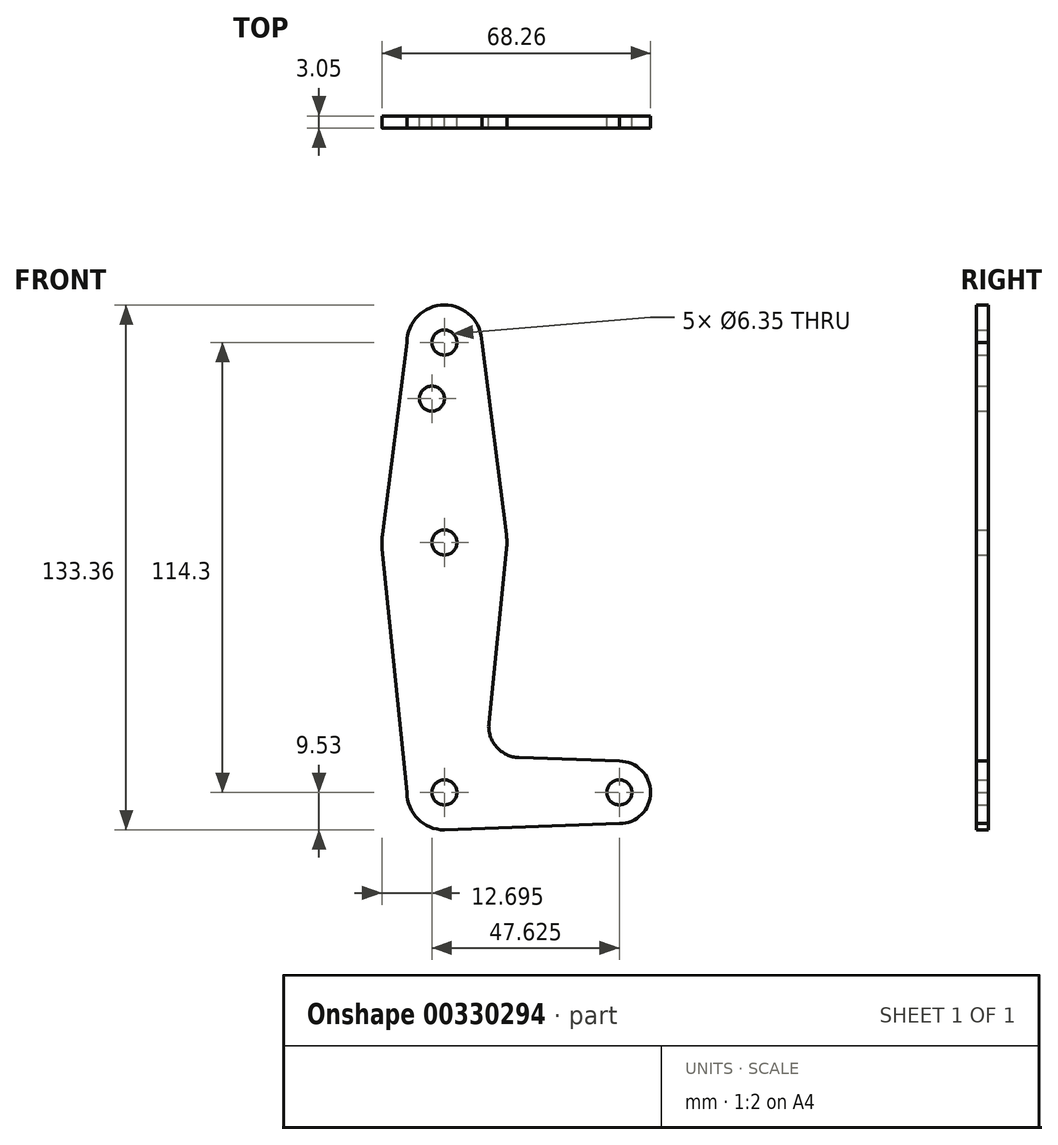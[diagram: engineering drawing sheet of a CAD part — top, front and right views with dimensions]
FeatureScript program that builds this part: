
annotation { "Feature Type Name" : "Feature", "Feature Type Description" : "" }
export const myFeature = defineFeature(function(context is Context, id is Id, definition is map)
    precondition{}
    {
        {
            var Q0;
            Q0=qCreatedBy(makeId("Front.planeOp"),FACE);
            var sketch = newSketch(context, id + "F0", { "sketchPlane" : qUnion([Q0])});
            skLineSegment(sketch, "E0", {"start": v(0, 0) * mm, "end": v(0, 114.3) * mm, "construction": true});
            skLineSegment(sketch, "E1", {"start": v(0, 0) * mm, "end": v(44.45, 0) * mm, "construction": true});
            skCircle(sketch, "E2", {"center": v(0, 0) * mm, "radius": 9.53 * mm});
            skCircle(sketch, "E3", {"center": v(44.45, 0) * mm, "radius": 7.94 * mm});
            skCircle(sketch, "E4", {"center": v(0, 114.3) * mm, "radius": 9.53 * mm});
            skCircle(sketch, "E5", {"center": v(0, 63.5) * mm, "radius": 15.88 * mm});
            skLineSegment(sketch, "E6", {"start": v(18.93, 8.85) * mm, "end": v(44.45, 7.94) * mm});
            skLineSegment(sketch, "E7", {"start": v(0, -9.52) * mm, "end": v(44.45, -7.94) * mm});
            skLineSegment(sketch, "E8", {"start": v(-9.53, 0) * mm, "end": v(-15.8, 61.9) * mm});
            skLineSegment(sketch, "E9", {"start": v(11.3, 17.6) * mm, "end": v(15.8, 61.9) * mm});
            skLineSegment(sketch, "E10", {"start": v(-9.53, 114.3) * mm, "end": v(-15.75, 65.5) * mm});
            skLineSegment(sketch, "E11", {"start": v(9.53, 114.3) * mm, "end": v(15.75, 65.5) * mm});
            skCircle(sketch, "E12", {"center": v(0, 114.3) * mm, "radius": 3.18 * mm});
            skCircle(sketch, "E13", {"center": v(0, 63.5) * mm, "radius": 3.18 * mm});
            skCircle(sketch, "E14", {"center": v(0, 0) * mm, "radius": 3.18 * mm});
            skCircle(sketch, "E15", {"center": v(44.45, 0) * mm, "radius": 3.18 * mm});
            skArc(sketch, "E16.filletArc", {"start": v(11.3, 17.6) * mm, "mid": v(13.22, 11.57) * mm, "end": v(18.93, 8.85) * mm});
            skCircle(sketch, "E17", {"center": v(-3.18, 100.03) * mm, "radius": 3.18 * mm});
            skSolve(sketch);
        }
        {
            var Q0;
            Q0=makeQuery(id+"F0.imprint","IMPRINT",FACE,{"disambiguationData":[TD([[makeQuery(id+"F0.imprint","IMPRINT",EDGE,{"derivedFrom":sQuery(id+"F0.wireOp",EDGE,"E12")}),-1.0]])]});
            var Q1;
            {var subQ1=sQuery(id+"F0.wireOp",EDGE,"E10");Q1=makeQuery(id+"F0.imprint","IMPRINT",FACE,{"disambiguationData":[TD([[makeQuery(id+"F0.imprint","IMPRINT",EDGE,{"derivedFrom":subQ1}),1.0]])]});}
            var Q2;
            Q2=makeQuery(id+"F0.imprint","IMPRINT",FACE,{"disambiguationData":[TD([[makeQuery(id+"F0.imprint","IMPRINT",EDGE,{"derivedFrom":sQuery(id+"F0.wireOp",EDGE,"E13")}),-1.0]])]});
            var Q3;
            {var subQ0=sQuery(id+"F0.wireOp",EDGE,"E6");Q3=makeQuery(id+"F0.imprint","IMPRINT",FACE,{"disambiguationData":[TD([[makeQuery(id+"F0.imprint","IMPRINT",EDGE,{"derivedFrom":subQ0}),-1.0]])]});}
            var Q4;
            Q4=makeQuery(id+"F0.imprint","IMPRINT",FACE,{"disambiguationData":[TD([[makeQuery(id+"F0.imprint","IMPRINT",EDGE,{"derivedFrom":sQuery(id+"F0.wireOp",EDGE,"E15")}),-1.0]])]});
            var Q5;
            Q5=makeQuery(id+"F0.imprint","IMPRINT",FACE,{"disambiguationData":[TD([[makeQuery(id+"F0.imprint","IMPRINT",EDGE,{"derivedFrom":sQuery(id+"F0.wireOp",EDGE,"E14")}),-1.0]])]});
            extrude(context, id + "F1", {"entities" : qUnion([Q0, Q1, Q2, Q3, Q4, Q5]), "depth" : 3.05 * mm});
        }
    });
